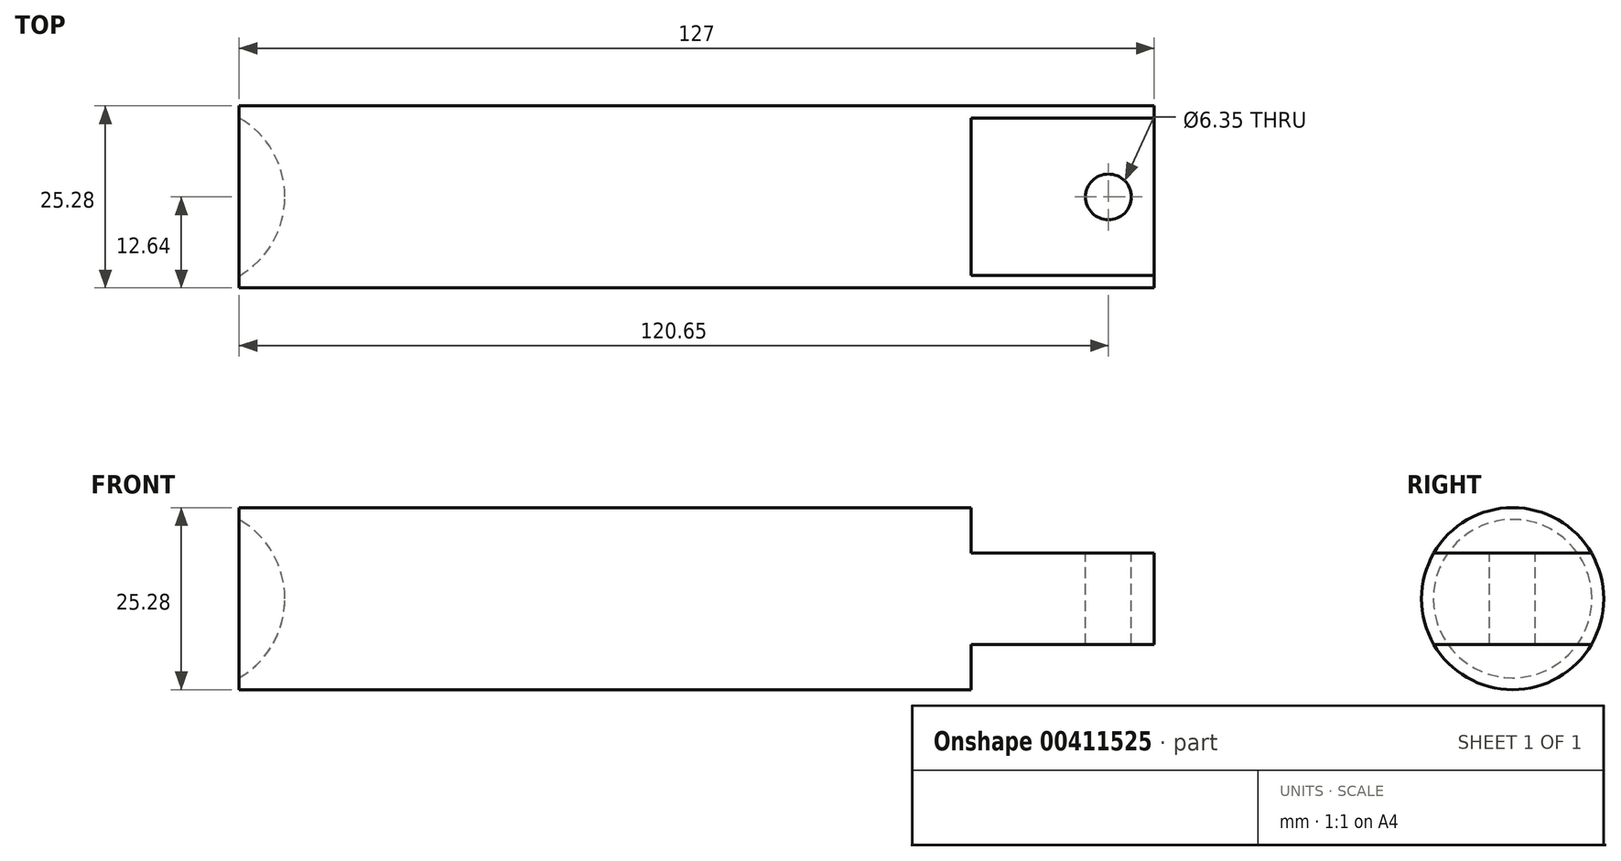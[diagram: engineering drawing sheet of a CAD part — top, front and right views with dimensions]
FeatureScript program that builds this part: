
annotation { "Feature Type Name" : "Feature", "Feature Type Description" : "" }
export const myFeature = defineFeature(function(context is Context, id is Id, definition is map)
    precondition{}
    {
        {
            var Q0;
            Q0=qCreatedBy(makeId("Right.planeOp"),FACE);
            var sketch = newSketch(context, id + "F0", { "sketchPlane" : qUnion([Q0])});
            skCircle(sketch, "E0", {"center": v(0, 0) * mm, "radius": 12.64 * mm});
            skSolve(sketch);
        }
        {
            var Q0;
            Q0 = qSketchRegion(id + "F0", true);
            extrude(context, id + "F1", {"entities" : qUnion([Q0]), "depth" : 127 * mm});
        }
        {
            var Q0;
            Q0=qCreatedBy(makeId("Front.planeOp"),FACE);
            var sketch = newSketch(context, id + "F2", { "sketchPlane" : qUnion([Q0])});
            skLineSegment(sketch, "E1.bottom", {"start": v(101.6, 12.87) * mm, "end": v(127, 12.87) * mm});
            skLineSegment(sketch, "E1.top", {"start": v(101.6, 6.35) * mm, "end": v(127, 6.35) * mm});
            skLineSegment(sketch, "E1.left", {"start": v(101.6, 12.87) * mm, "end": v(101.6, 6.35) * mm});
            skLineSegment(sketch, "E1.right", {"start": v(127, 12.87) * mm, "end": v(127, 6.35) * mm});
            skLineSegment(sketch, "E2.bottom", {"start": v(101.6, -12.64) * mm, "end": v(127, -12.64) * mm});
            skLineSegment(sketch, "E2.top", {"start": v(101.6, -6.35) * mm, "end": v(127, -6.35) * mm});
            skLineSegment(sketch, "E2.left", {"start": v(101.6, -12.64) * mm, "end": v(101.6, -6.35) * mm});
            skLineSegment(sketch, "E2.right", {"start": v(127, -12.64) * mm, "end": v(127, -6.35) * mm});
            skSolve(sketch);
        }
        {
            var Q0;
            Q0 = qSketchRegion(id + "F2", true);
            extrude(context, id + "F3", {"entities" : qUnion([Q0]), "operationType" : NewBodyOperationType.REMOVE, "oppositeDirection" : true, "depth" : 127 * mm});
        }
        {
            var Q0;
            Q0 = qSketchRegion(id + "F2", true);
            extrude(context, id + "F4", {"entities" : qUnion([Q0]), "operationType" : NewBodyOperationType.REMOVE, "depth" : 25.4 * mm});
        }
        {
            var Q0;
            Q0=qCreatedBy(makeId("Front.planeOp"),FACE);
            var sketch = newSketch(context, id + "F5", { "sketchPlane" : qUnion([Q0])});
            skArc(sketch, "E3", {"start": v(-19.05, 0) * mm, "mid": v(-6.35, -12.7) * mm, "end": v(6.35, 0) * mm});
            skLineSegment(sketch, "E4", {"start": v(-19.05, 0) * mm, "end": v(6.35, 0) * mm});
            skSolve(sketch);
        }
        {
            var Q0;
            Q0 = qSketchRegion(id + "F5", true);
            var Q1;
            Q1=sQuery(id+"F5.wireOp",EDGE,"E4");
            revolve(context, id + "F6", {"operationType" : NewBodyOperationType.REMOVE, "entities" : qUnion([Q0]), "axis" : qUnion([Q1]), "revolveType" : RevolveType.FULL, "oppositeDirection" : true});
        }
        {
            var Q0;
            {var subQ0=sQuery(id+"F2.wireOp",EDGE,"E1.top");Q0=makeQuery(id+"F4.boolean.opBoolean","MERGE",FACE,{"derivedFrom":[makeQuery(id+"F3.boolean.opBoolean","COPY",FACE,{"derivedFrom":makeQuery(id+"F3.opExtrude","SWEPT_FACE",FACE,{"disambiguationData":[OSD([subQ0])]})}),makeQuery(id+"F4.opExtrude","SWEPT_FACE",FACE,{"disambiguationData":[OSD([subQ0])]})]});}
            var sketch = newSketch(context, id + "F7", { "sketchPlane" : qUnion([Q0])});
            skCircle(sketch, "E5", {"center": v(120.65, 0) * mm, "radius": 3.18 * mm});
            skSolve(sketch);
        }
        {
            var Q0;
            Q0 = qSketchRegion(id + "F7", true);
            extrude(context, id + "F8", {"entities" : qUnion([Q0]), "operationType" : NewBodyOperationType.REMOVE, "oppositeDirection" : true, "depth" : 25.4 * mm});
        }
    });
